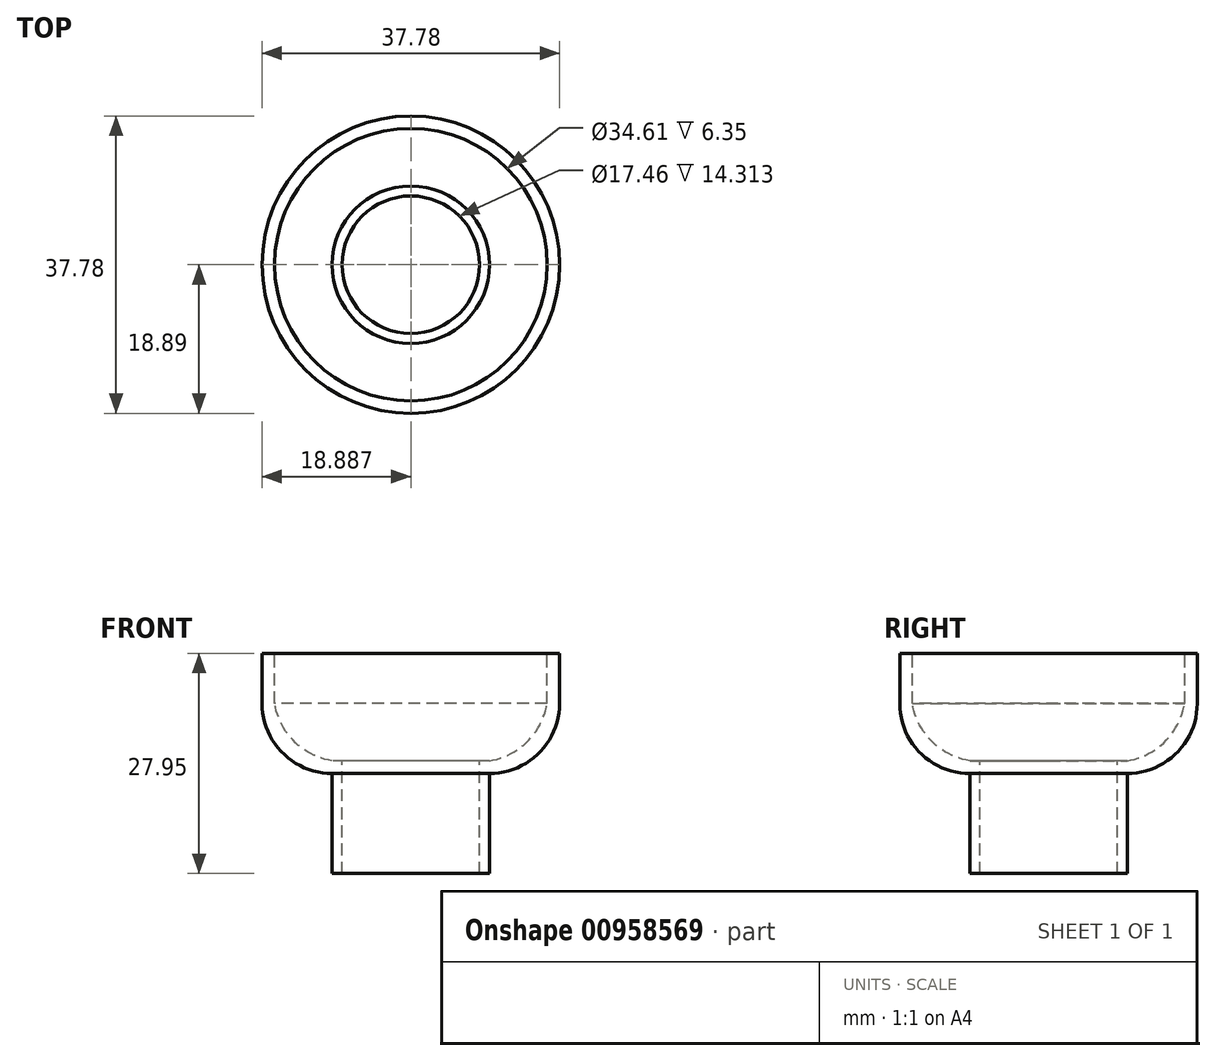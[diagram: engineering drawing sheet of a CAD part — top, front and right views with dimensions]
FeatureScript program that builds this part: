
annotation { "Feature Type Name" : "Feature", "Feature Type Description" : "" }
export const myFeature = defineFeature(function(context is Context, id is Id, definition is map)
    precondition{}
    {
        {
            var Q0;
            Q0=qCreatedBy(makeId("Front.planeOp"),FACE);
            var sketch = newSketch(context, id + "F0", { "sketchPlane" : qUnion([Q0])});
            skLineSegment(sketch, "E0", {"start": v(-10.95, 0) * mm, "end": v(-10.95, -6.35) * mm});
            skLineSegment(sketch, "E1", {"start": v(-2.06, -15.24) * mm, "end": v(-0.8, -15.24) * mm});
            skPoint(sketch, "E2.visualSharp", {"position": v(-10.95, -15.24) * mm});
            skArc(sketch, "E2.filletArc", {"start": v(-10.95, -6.35) * mm, "mid": v(-8.35, -12.64) * mm, "end": v(-2.06, -15.24) * mm});
            skLineSegment(sketch, "E3", {"start": v(-10.95, 0) * mm, "end": v(-9.37, 0) * mm});
            skLineSegment(sketch, "E4", {"start": v(-9.37, 0) * mm, "end": v(-9.37, -6.35) * mm});
            skArc(sketch, "E5", {"start": v(-9.37, -6.35) * mm, "mid": v(-6.88, -11.16) * mm, "end": v(-2.06, -13.64) * mm});
            skLineSegment(sketch, "E6", {"start": v(-2.06, -13.64) * mm, "end": v(-0.8, -13.64) * mm});
            skLineSegment(sketch, "E7", {"start": v(-0.8, -15.24) * mm, "end": v(-0.8, -13.64) * mm});
            skLineSegment(sketch, "E8", {"start": v(-0.8, -15.24) * mm, "end": v(-0.8, -27.95) * mm});
            skLineSegment(sketch, "E9", {"start": v(0, 0) * mm, "end": v(7.94, 0) * mm});
            skLineSegment(sketch, "E10", {"start": v(7.94, 0) * mm, "end": v(7.94, -27.95) * mm});
            skLineSegment(sketch, "E11", {"start": v(-0.8, -27.95) * mm, "end": v(7.94, -27.95) * mm});
            skLineSegment(sketch, "E12", {"start": v(-0.8, -27.95) * mm, "end": v(-2.06, -27.95) * mm});
            skLineSegment(sketch, "E13", {"start": v(-2.06, -27.95) * mm, "end": v(-2.06, -13.64) * mm});
            skSolve(sketch);
        }
        {
            var Q0;
            Q0=makeQuery(id+"F0.imprint","IMPRINT",FACE,{"disambiguationData":[TD([[makeQuery(id+"F0.imprint","IMPRINT",EDGE,{"derivedFrom":sQuery(id+"F0.wireOp",EDGE,"E0")}),1.0]])]});
            var Q1;
            {var subQ0=sQuery(id+"F0.wireOp",EDGE,"E1");Q1=makeQuery(id+"F0.imprint","IMPRINT",FACE,{"disambiguationData":[TD([[makeQuery(id+"F0.imprint","IMPRINT",EDGE,{"derivedFrom":subQ0}),1.0]])]});}
            var Q2;
            {var subQ0=sQuery(id+"F0.wireOp",EDGE,"E1");Q2=makeQuery(id+"F0.imprint","IMPRINT",FACE,{"disambiguationData":[TD([[makeQuery(id+"F0.imprint","IMPRINT",EDGE,{"derivedFrom":subQ0}),-1.0]])]});}
            var Q3;
            Q3=sQuery(id+"F0.wireOp",EDGE,"E10");
            revolve(context, id + "F1", {"surfaceOperationType" : NewSurfaceOperationType.NEW, "entities" : qUnion([Q0, Q1, Q2]), "axis" : qUnion([Q3]), "revolveType" : RevolveType.FULL});
        }
    });
